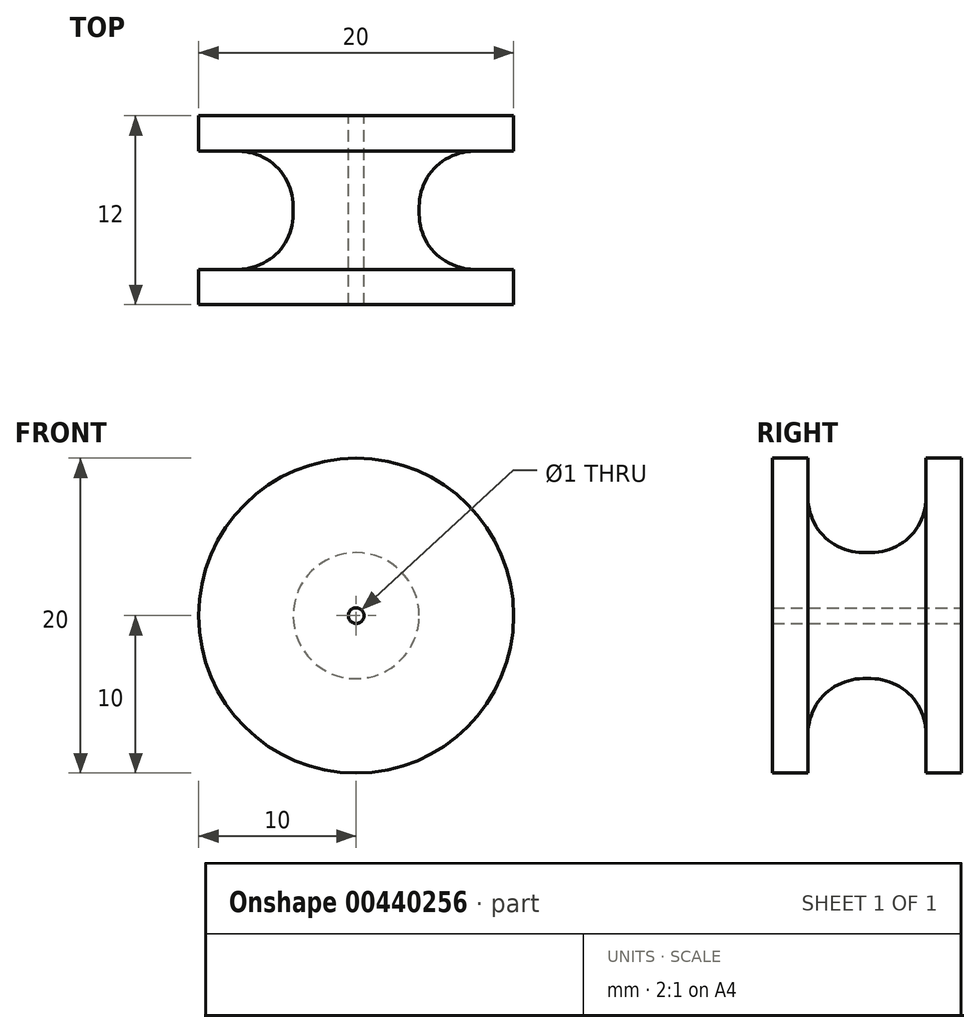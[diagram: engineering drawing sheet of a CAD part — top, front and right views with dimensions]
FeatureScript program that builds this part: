
annotation { "Feature Type Name" : "Feature", "Feature Type Description" : "" }
export const myFeature = defineFeature(function(context is Context, id is Id, definition is map)
    precondition{}
    {
        {
            var Q0;
            Q0=qCreatedBy(makeId("Front.planeOp"),FACE);
            var sketch = newSketch(context, id + "F0", { "sketchPlane" : qUnion([Q0])});
            skCircle(sketch, "E0", {"center": v(0, 0) * mm, "radius": 10 * mm});
            skSolve(sketch);
        }
        {
            var Q0;
            Q0=makeQuery(id+"F0.imprint","IMPRINT",FACE,{"disambiguationData":[TD([[makeQuery(id+"F0.imprint","IMPRINT",EDGE,{"derivedFrom":sQuery(id+"F0.wireOp",EDGE,"E0")}),1.0]])]});
            var Q1;
            Q1=sQuery(id+"F0.wireOp",EDGE,"E0");
            extrude(context, id + "F1", {"entities" : qUnion([Q0]), "surfaceEntities" : qUnion([Q1]), "endBound" : BoundingType.SYMMETRIC, "depth" : 12 * mm});
        }
        {
            var Q0;
            Q0=qCreatedBy(makeId("Top.planeOp"),FACE);
            var sketch = newSketch(context, id + "F2", { "sketchPlane" : qUnion([Q0])});
            skLineSegment(sketch, "E1", {"start": v(0, 41) * mm, "end": v(0, -41.3) * mm});
            skSolve(sketch);
        }
        {
            var Q0;
            Q0=qCreatedBy(makeId("Right.planeOp"),FACE);
            var sketch = newSketch(context, id + "F3", { "sketchPlane" : qUnion([Q0])});
            skLineSegment(sketch, "E2.bottom", {"start": v(-3.75, 10) * mm, "end": v(3.75, 10) * mm});
            skLineSegment(sketch, "E2.top", {"start": v(-0.25, 4) * mm, "end": v(0.25, 4) * mm});
            skLineSegment(sketch, "E2.left", {"start": v(-3.75, 10) * mm, "end": v(-3.75, 7.5) * mm});
            skLineSegment(sketch, "E2.right", {"start": v(3.75, 10) * mm, "end": v(3.75, 7.5) * mm});
            skPoint(sketch, "E3.visualSharp", {"position": v(-3.75, 4) * mm});
            skArc(sketch, "E3.filletArc", {"start": v(-3.75, 7.5) * mm, "mid": v(-2.72, 5.03) * mm, "end": v(-0.25, 4) * mm});
            skPoint(sketch, "E4.visualSharp", {"position": v(3.75, 4) * mm});
            skArc(sketch, "E4.filletArc", {"start": v(0.25, 4) * mm, "mid": v(2.72, 5.03) * mm, "end": v(3.75, 7.5) * mm});
            skSolve(sketch);
        }
        {
            var Q0;
            Q0=qSketchRegion(id+"F3",true);
            var Q1;
            Q1=sQuery(id+"F2.wireOp",EDGE,"E1");
            revolve(context, id + "F4", {"operationType" : NewBodyOperationType.REMOVE, "entities" : qUnion([Q0]), "axis" : qUnion([Q1]), "revolveType" : RevolveType.FULL, "oppositeDirection" : true});
        }
        {
            var Q0;
            Q0=makeQuery(id+"F1.opExtrude","CAP_FACE",FACE,{"disambiguationData":[OSD([sQuery(id+"F0.wireOp",EDGE,"E0")])],"isStart":true});
            var sketch = newSketch(context, id + "F5", { "sketchPlane" : qUnion([Q0])});
            skCircle(sketch, "E5", {"center": v(0, 0) * mm, "radius": 0.5 * mm});
            skSolve(sketch);
        }
        {
            var Q0;
            Q0=makeQuery(id+"F5.imprint","IMPRINT",FACE,{"disambiguationData":[TD([[makeQuery(id+"F5.imprint","IMPRINT",EDGE,{"derivedFrom":sQuery(id+"F5.wireOp",EDGE,"E5")}),1.0]])]});
            var Q1;
            Q1=sQuery(id+"F5.wireOp",EDGE,"E5");
            extrude(context, id + "F6", {"entities" : qUnion([Q0]), "operationType" : NewBodyOperationType.REMOVE, "surfaceEntities" : qUnion([Q1]), "endBound" : BoundingType.THROUGH_ALL, "oppositeDirection" : true, "depth" : 25 * mm});
        }
    });
